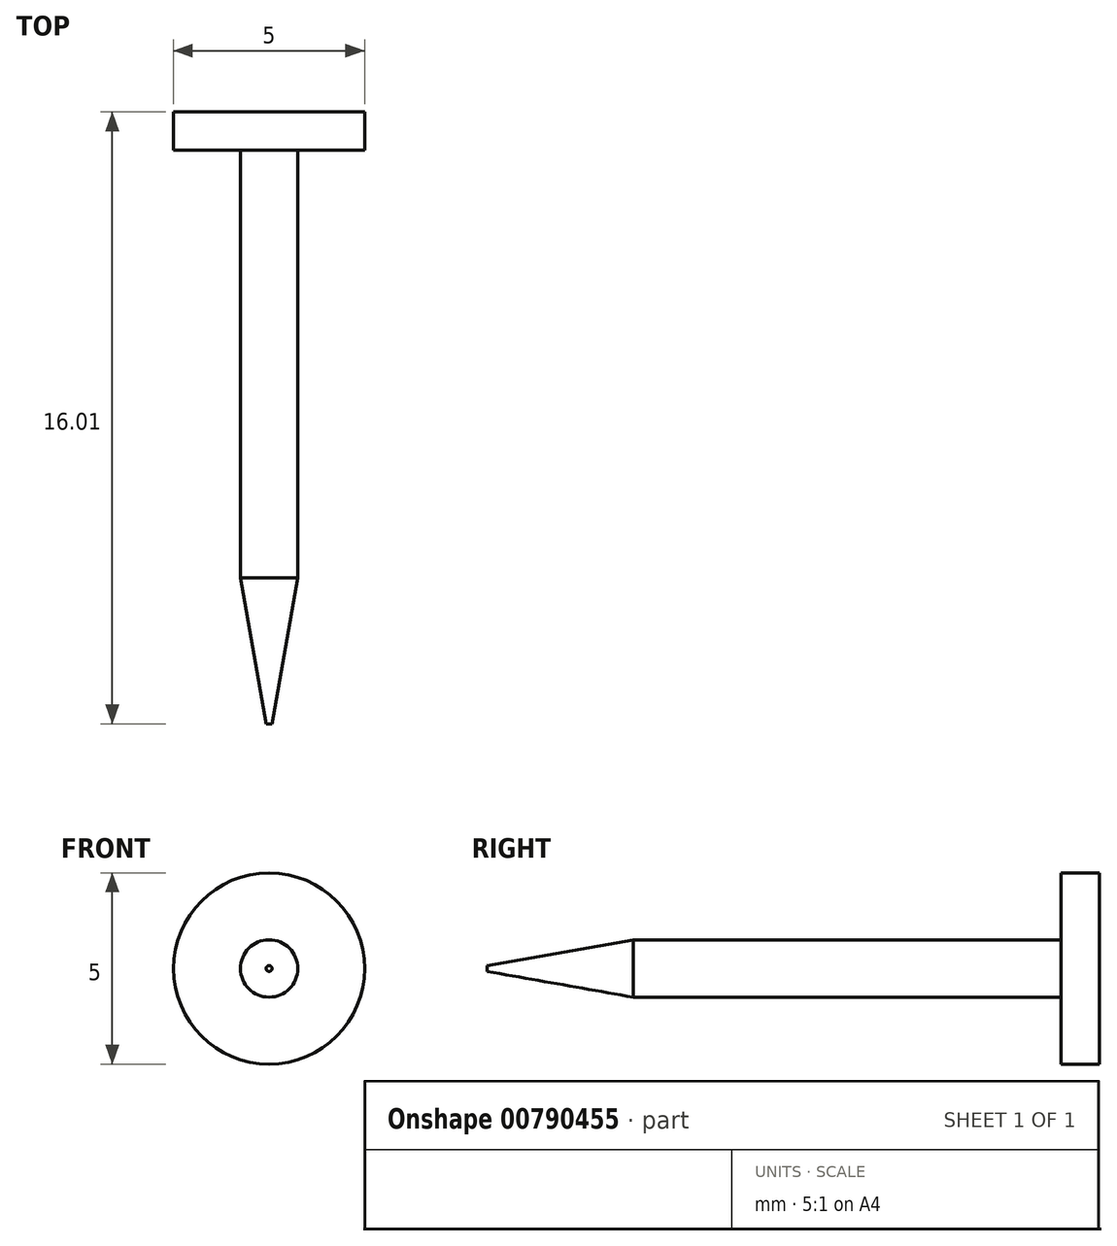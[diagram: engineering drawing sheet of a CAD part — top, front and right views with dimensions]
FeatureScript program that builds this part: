
annotation { "Feature Type Name" : "Feature", "Feature Type Description" : "" }
export const myFeature = defineFeature(function(context is Context, id is Id, definition is map)
    precondition{}
    {
        {
            var Q0;
            Q0=qCreatedBy(makeId("Top.planeOp"),FACE);
            var sketch = newSketch(context, id + "F0", { "sketchPlane" : qUnion([Q0])});
            skLineSegment(sketch, "E0.bottom", {"start": v(0, 52.82) * mm, "end": v(2.5, 52.82) * mm});
            skLineSegment(sketch, "E0.top", {"start": v(0, 51.82) * mm, "end": v(2.5, 51.82) * mm});
            skLineSegment(sketch, "E0.left", {"start": v(0, 52.82) * mm, "end": v(0, 51.82) * mm});
            skLineSegment(sketch, "E0.right", {"start": v(2.5, 52.82) * mm, "end": v(2.5, 51.82) * mm});
            skLineSegment(sketch, "E1", {"start": v(0, 36.81) * mm, "end": v(0, 76.81) * mm, "construction": true});
            skLineSegment(sketch, "E2", {"start": v(0, 51.82) * mm, "end": v(0, 36.81) * mm});
            skLineSegment(sketch, "E3", {"start": v(0.75, 40.64) * mm, "end": v(0.75, 51.82) * mm});
            skLineSegment(sketch, "E4", {"start": v(0, 36.81) * mm, "end": v(0.08, 36.81) * mm});
            skLineSegment(sketch, "E5", {"start": v(0.75, 40.64) * mm, "end": v(0.08, 36.81) * mm});
            skSolve(sketch);
        }
        {
            var Q0;
            {var subQ0=sQuery(id+"F0.wireOp",EDGE,"E2");Q0=makeQuery(id+"F0.imprint","IMPRINT",FACE,{"disambiguationData":[TD([[makeQuery(id+"F0.imprint","IMPRINT",EDGE,{"derivedFrom":subQ0}),1.0]])]});}
            var Q1;
            Q1=makeQuery(id+"F0.imprint","IMPRINT",FACE,{"disambiguationData":[TD([[makeQuery(id+"F0.imprint","IMPRINT",EDGE,{"derivedFrom":sQuery(id+"F0.wireOp",EDGE,"E0.bottom")}),-1.0]])]});
            var Q2;
            Q2=sQuery(id+"F0.wireOp",EDGE,"E1");
            revolve(context, id + "F1", {"surfaceOperationType" : NewSurfaceOperationType.NEW, "entities" : qUnion([Q0, Q1]), "axis" : qUnion([Q2]), "revolveType" : RevolveType.FULL});
        }
    });
